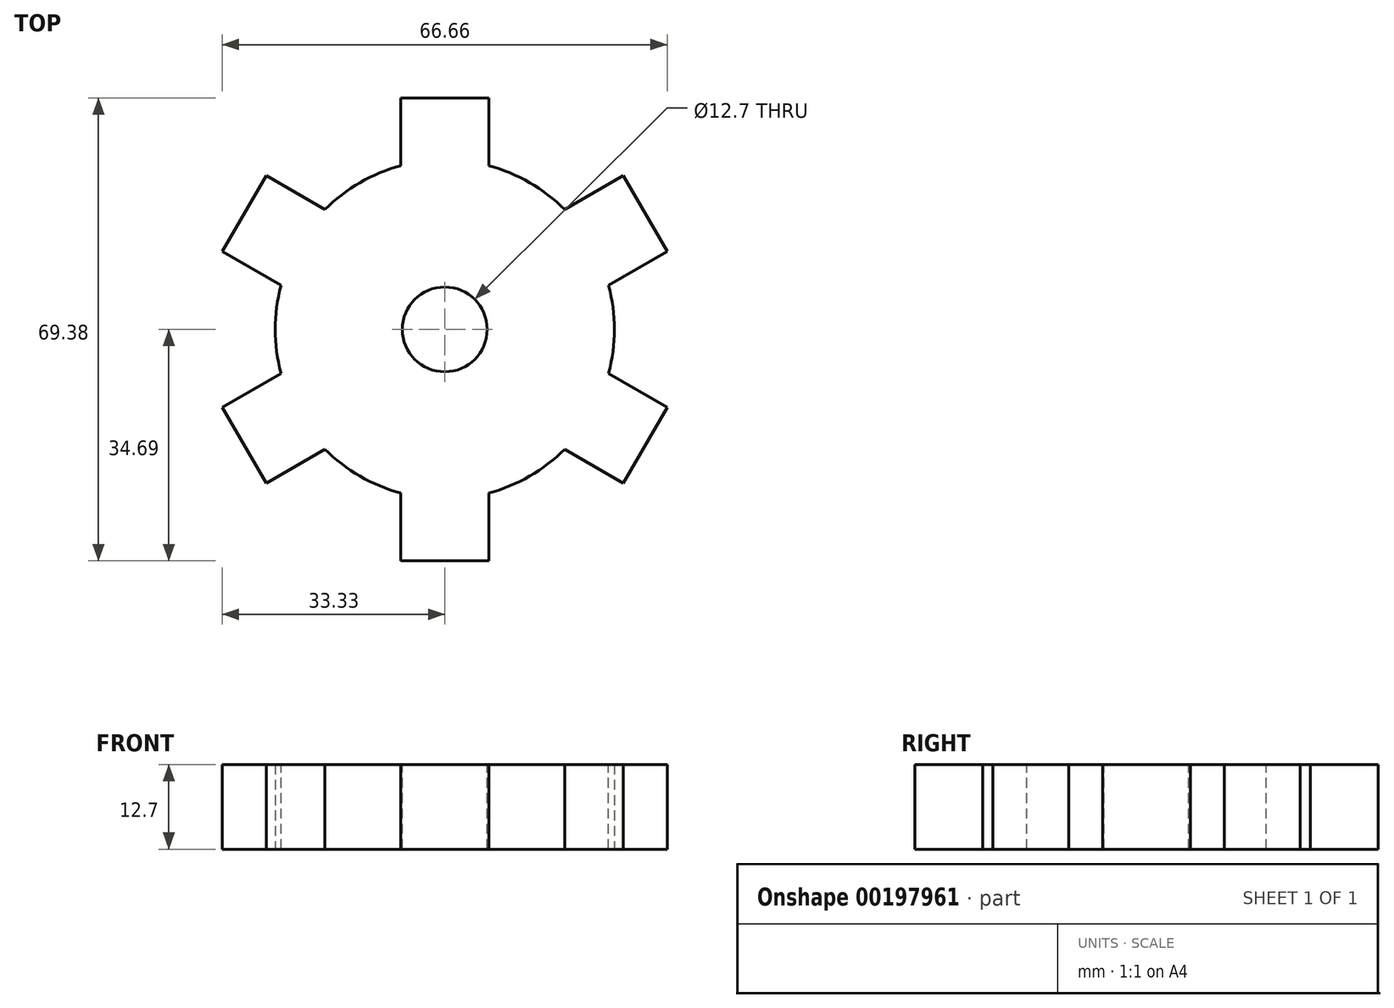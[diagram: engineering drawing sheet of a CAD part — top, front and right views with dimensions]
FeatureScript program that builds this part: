
annotation { "Feature Type Name" : "Feature", "Feature Type Description" : "" }
export const myFeature = defineFeature(function(context is Context, id is Id, definition is map)
    precondition{}
    {
        {
            var Q0;
            Q0=qCreatedBy(makeId("Top.planeOp"),FACE);
            var sketch = newSketch(context, id + "F0", { "sketchPlane" : qUnion([Q0])});
            skCircle(sketch, "E0", {"center": v(0, 0) * mm, "radius": 25.4 * mm});
            skSolve(sketch);
        }
        {
            var Q0;
            Q0=makeQuery(id+"F0.imprint","IMPRINT",FACE,{"disambiguationData":[TD([[makeQuery(id+"F0.imprint","IMPRINT",EDGE,{"derivedFrom":sQuery(id+"F0.wireOp",EDGE,"E0")}),1.0]])]});
            extrude(context, id + "F1", {"entities" : qUnion([Q0]), "depth" : 12.7 * mm});
        }
        {
            var Q0;
            Q0=makeQuery(id+"F1.opExtrude","CAP_FACE",FACE,{"disambiguationData":[OSD([sQuery(id+"F0.wireOp",EDGE,"E0")])],"isStart":false});
            var sketch = newSketch(context, id + "F2", { "sketchPlane" : qUnion([Q0])});
            skLineSegment(sketch, "E1", {"start": v(0, 0) * mm, "end": v(0, 25.4) * mm});
            skLineSegment(sketch, "E2", {"start": v(0, 0) * mm, "end": v(6.57, -24.53) * mm});
            skLineSegment(sketch, "E3", {"start": v(0, 0) * mm, "end": v(-6.57, -24.53) * mm});
            skLineSegment(sketch, "E4", {"start": v(6.57, -24.53) * mm, "end": v(-6.57, -24.53) * mm});
            skLineSegment(sketch, "E5.0", {"start": v(6.57, -34.7) * mm, "end": v(-6.57, -34.7) * mm});
            skLineSegment(sketch, "E6", {"start": v(-6.57, -24.53) * mm, "end": v(-6.57, -34.7) * mm});
            skLineSegment(sketch, "E7", {"start": v(6.57, -24.53) * mm, "end": v(6.57, -34.7) * mm});
            skSolve(sketch);
        }
        {
            var Q0;
            Q0=makeQuery(id+"F2.imprint","IMPRINT",FACE,{"disambiguationData":[TD([[makeQuery(id+"F2.imprint","IMPRINT",EDGE,{"derivedFrom":sQuery(id+"F2.wireOp",EDGE,"E5.0")}),-1.0]])]});
            extrude(context, id + "F3", {"entities" : qUnion([Q0]), "operationType" : NewBodyOperationType.ADD, "oppositeDirection" : true, "depth" : 12.7 * mm});
        }
        {
            var Q0;
            Q0=qCreatedBy(makeId("Front.planeOp"),FACE);
            var sketch = newSketch(context, id + "F4", { "sketchPlane" : qUnion([Q0])});
            skLineSegment(sketch, "E8", {"start": v(0, 0) * mm, "end": v(0, -60.26) * mm});
            skSolve(sketch);
        }
        {
            var Q0;
            Q0=makeQuery(id+"F1.opExtrude","SWEPT_BODY",BODY,{"disambiguationData":[OSD([sQuery(id+"F0.wireOp",EDGE,"E0")])]});
            var Q1;
            Q1=sQuery(id+"F4.wireOp",EDGE,"E8");
            circularPattern(context, id + "F5", {"operationType" : NewBodyOperationType.ADD, "entities" : qUnion([Q0]), "axis" : qUnion([Q1]), "angle" : 360 * degree, "instanceCount" : 6, "equalSpace" : true});
        }
        {
            var Q0;
            {var subQ0=sQuery(id+"F0.wireOp",EDGE,"E0");var subQ1=makeQuery(id+"F3.boolean.opBoolean","MERGE",FACE,{"derivedFrom":[makeQuery(id+"F1.opExtrude","CAP_FACE",FACE,{"disambiguationData":[OSD([subQ0])],"isStart":false}),makeQuery(id+"F3.opExtrude","CAP_FACE",FACE,{"disambiguationData":[OSD([subQ0,sQuery(id+"F2.wireOp",EDGE,"E5.0"),sQuery(id+"F2.wireOp",EDGE,"E6"),sQuery(id+"F2.wireOp",EDGE,"E7")])],"isStart":true})]});Q0=makeQuery(id+"F5.boolean.opBoolean","MERGE",FACE,{"derivedFrom":[subQ1,makeQuery(id+"F5.opPattern","COPY",FACE,{"derivedFrom":subQ1,"instanceName":"1"}),makeQuery(id+"F5.opPattern","COPY",FACE,{"derivedFrom":subQ1,"instanceName":"2"}),makeQuery(id+"F5.opPattern","COPY",FACE,{"derivedFrom":subQ1,"instanceName":"3"}),makeQuery(id+"F5.opPattern","COPY",FACE,{"derivedFrom":subQ1,"instanceName":"4"}),makeQuery(id+"F5.opPattern","COPY",FACE,{"derivedFrom":subQ1,"instanceName":"5"})]});}
            var sketch = newSketch(context, id + "F6", { "sketchPlane" : qUnion([Q0])});
            skCircle(sketch, "E9", {"center": v(0, 0) * mm, "radius": 6.35 * mm});
            skSolve(sketch);
        }
        {
            var Q0;
            Q0=makeQuery(id+"F6.imprint","IMPRINT",FACE,{"disambiguationData":[TD([[makeQuery(id+"F6.imprint","IMPRINT",EDGE,{"derivedFrom":sQuery(id+"F6.wireOp",EDGE,"E9")}),1.0]])]});
            extrude(context, id + "F7", {"entities" : qUnion([Q0]), "operationType" : NewBodyOperationType.REMOVE, "oppositeDirection" : true, "depth" : 12.7 * mm});
        }
    });
